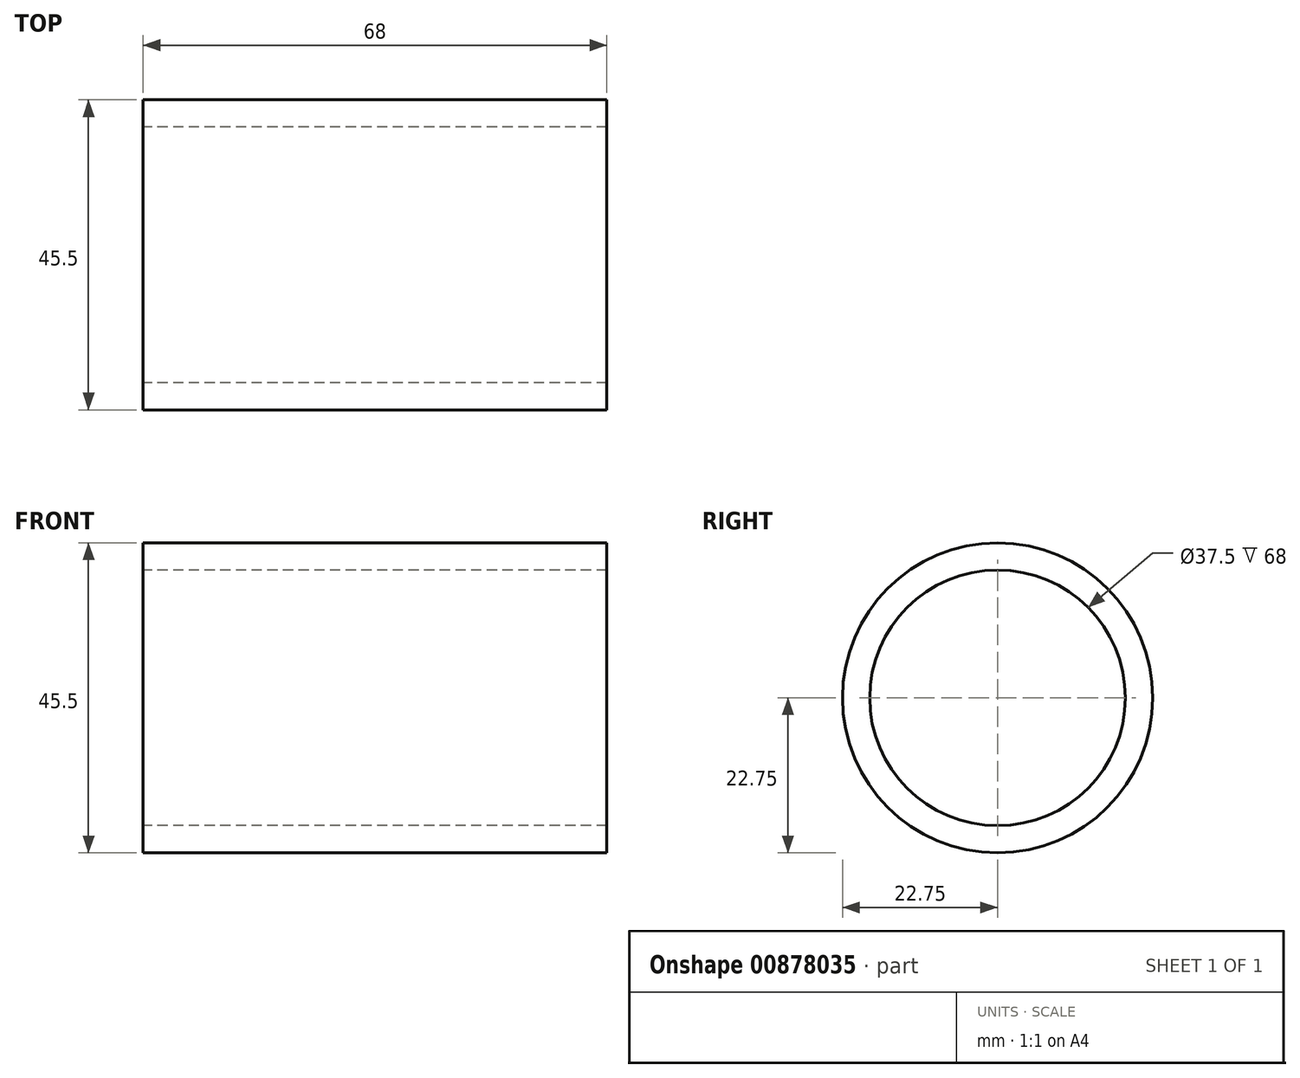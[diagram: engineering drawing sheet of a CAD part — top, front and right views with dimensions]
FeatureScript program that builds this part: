
annotation { "Feature Type Name" : "Feature", "Feature Type Description" : "" }
export const myFeature = defineFeature(function(context is Context, id is Id, definition is map)
    precondition{}
    {
        {
            var Q0;
            Q0=qCreatedBy(makeId("Right.planeOp"),FACE);
            var sketch = newSketch(context, id + "F0", { "sketchPlane" : qUnion([Q0])});
            skCircle(sketch, "E0", {"center": v(0, 0) * mm, "radius": 22.75 * mm});
            skCircle(sketch, "E1", {"center": v(0, 0) * mm, "radius": 18.75 * mm});
            skSolve(sketch);
        }
        {
            var Q0;
            Q0=makeQuery(id+"F0.imprint","IMPRINT",FACE,{"disambiguationData":[TD([[makeQuery(id+"F0.imprint","IMPRINT",EDGE,{"derivedFrom":sQuery(id+"F0.wireOp",EDGE,"E0")}),1.0]])]});
            extrude(context, id + "F1", {"entities" : qUnion([Q0]), "depth" : 68 * mm, "offsetDistance" : 25.4 * mm});
        }
    });
